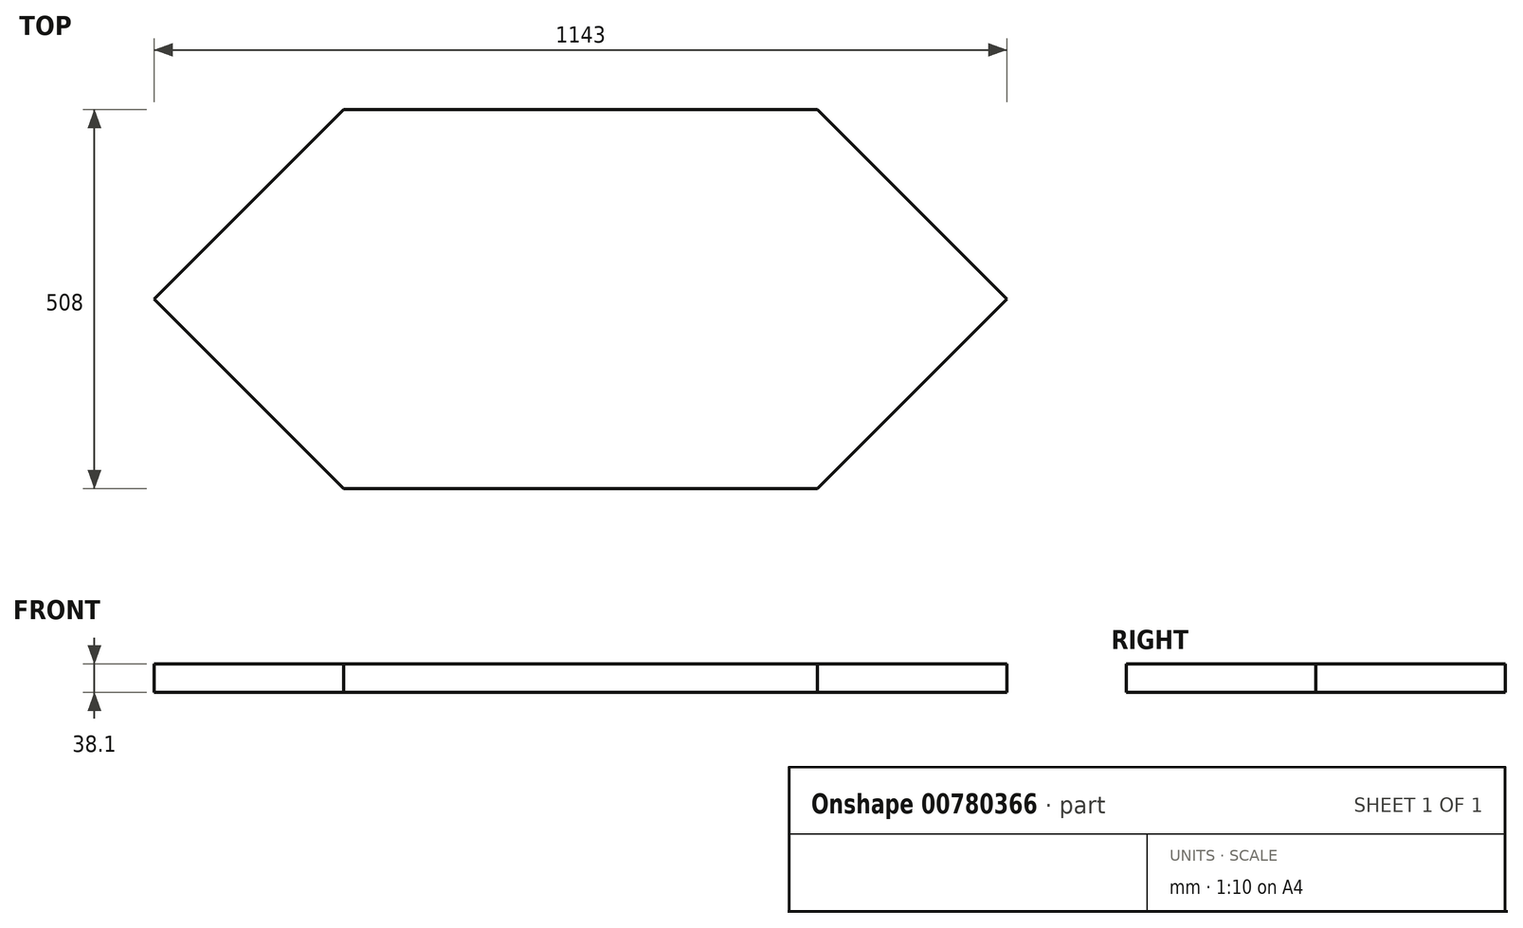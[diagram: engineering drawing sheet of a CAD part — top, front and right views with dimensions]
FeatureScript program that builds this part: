
annotation { "Feature Type Name" : "Feature", "Feature Type Description" : "" }
export const myFeature = defineFeature(function(context is Context, id is Id, definition is map)
    precondition{}
    {
        {
            var Q0;
            Q0=qCreatedBy(makeId("Top.planeOp"),FACE);
            var sketch = newSketch(context, id + "F0", { "sketchPlane" : qUnion([Q0])});
            skLineSegment(sketch, "E0", {"start": v(0, 0) * mm, "end": v(254, 254) * mm});
            skLineSegment(sketch, "E1", {"start": v(254, 254) * mm, "end": v(889, 254) * mm});
            skLineSegment(sketch, "E2", {"start": v(889, 254) * mm, "end": v(1143, 0) * mm});
            skLineSegment(sketch, "E3", {"start": v(0, 0) * mm, "end": v(1143, 0) * mm, "construction": true});
            skLineSegment(sketch, "E4.MirrorCS", {"start": v(0, 0) * mm, "end": v(254, -254) * mm});
            skLineSegment(sketch, "E5.MirrorCS", {"start": v(254, -254) * mm, "end": v(889, -254) * mm});
            skLineSegment(sketch, "E6.MirrorCS", {"start": v(889, -254) * mm, "end": v(1143, 0) * mm});
            skSolve(sketch);
        }
        {
            var Q0;
            Q0=makeQuery(id+"F0.imprint","IMPRINT",FACE,{"disambiguationData":[TD([[makeQuery(id+"F0.imprint","IMPRINT",EDGE,{"derivedFrom":sQuery(id+"F0.wireOp",EDGE,"E0")}),-1.0]])]});
            extrude(context, id + "F1", {"entities" : qUnion([Q0]), "depth" : 38.1 * mm, "offsetDistance" : 25.4 * mm});
        }
    });
